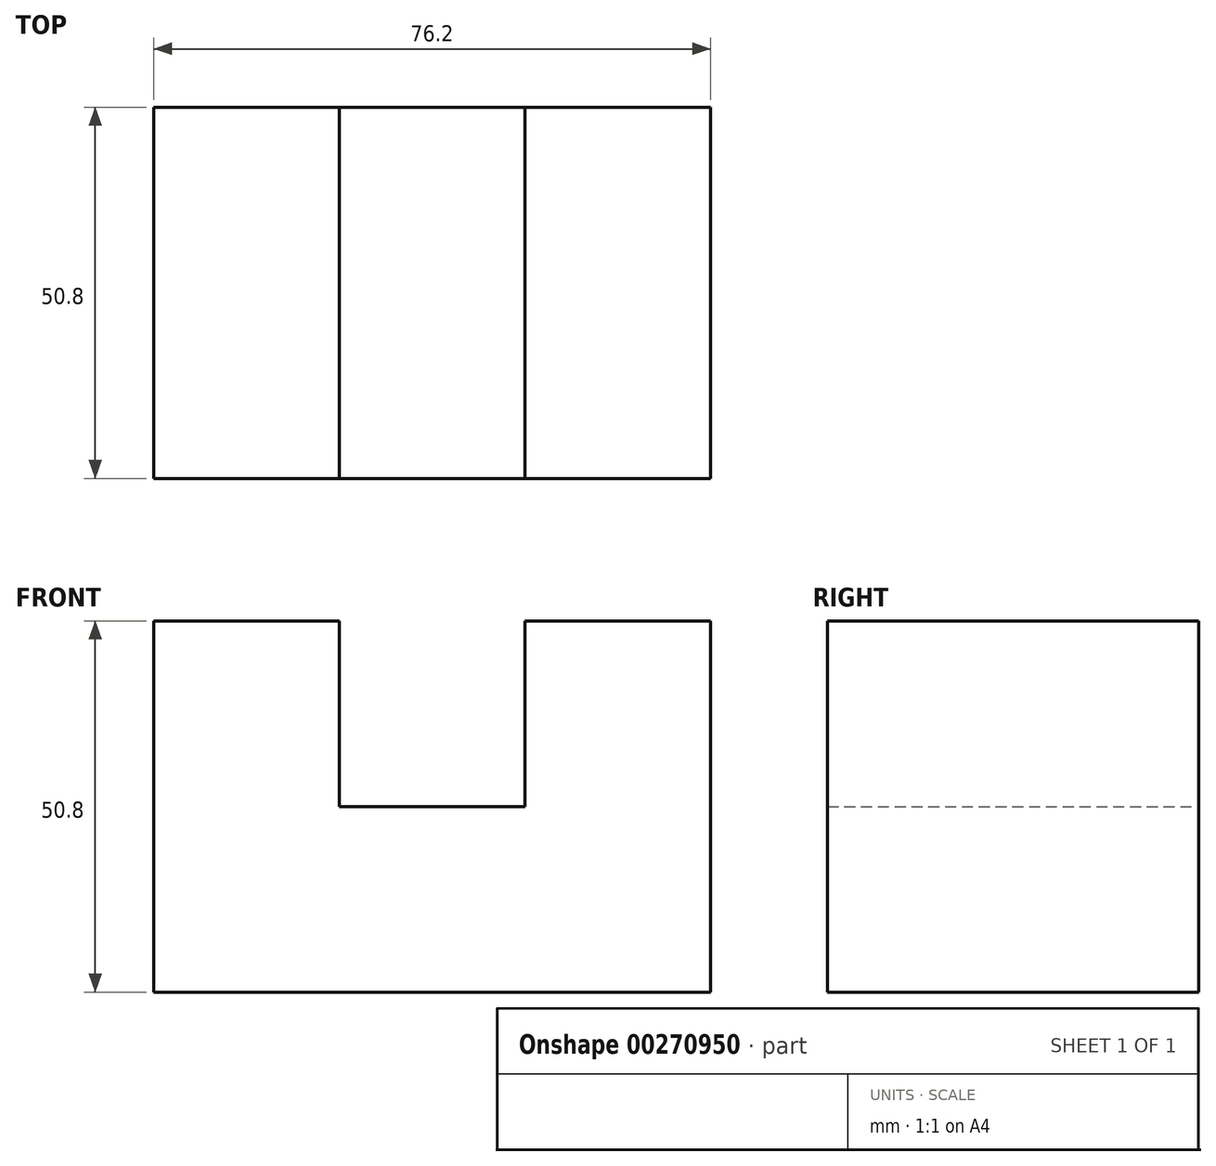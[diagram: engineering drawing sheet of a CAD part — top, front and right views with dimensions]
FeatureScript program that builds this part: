
annotation { "Feature Type Name" : "Feature", "Feature Type Description" : "" }
export const myFeature = defineFeature(function(context is Context, id is Id, definition is map)
    precondition{}
    {
        {
            var Q0;
            Q0=qCreatedBy(makeId("Front.planeOp"),FACE);
            var sketch = newSketch(context, id + "F0", { "sketchPlane" : qUnion([Q0])});
            skLineSegment(sketch, "E0", {"start": v(-68.55, 0) * mm, "end": v(-68.55, 50.8) * mm});
            skLineSegment(sketch, "E1", {"start": v(-68.55, 50.8) * mm, "end": v(-43.15, 50.8) * mm});
            skLineSegment(sketch, "E2", {"start": v(-43.15, 50.8) * mm, "end": v(-43.15, 25.4) * mm});
            skLineSegment(sketch, "E3", {"start": v(-43.15, 25.4) * mm, "end": v(-17.75, 25.4) * mm});
            skLineSegment(sketch, "E4", {"start": v(-17.75, 25.4) * mm, "end": v(-17.75, 50.8) * mm});
            skLineSegment(sketch, "E5", {"start": v(-17.75, 50.8) * mm, "end": v(7.65, 50.8) * mm});
            skLineSegment(sketch, "E6", {"start": v(7.65, 50.8) * mm, "end": v(7.65, 0) * mm});
            skLineSegment(sketch, "E7", {"start": v(-68.55, 0) * mm, "end": v(-17.75, 0) * mm});
            skLineSegment(sketch, "E8", {"start": v(-17.75, 0) * mm, "end": v(7.65, 0) * mm});
            skSolve(sketch);
        }
        {
            var Q0;
            Q0 = qSketchRegion(id + "F0", true);
            extrude(context, id + "F1", {"entities" : qUnion([Q0]), "depth" : 50.8 * mm});
        }
    });
